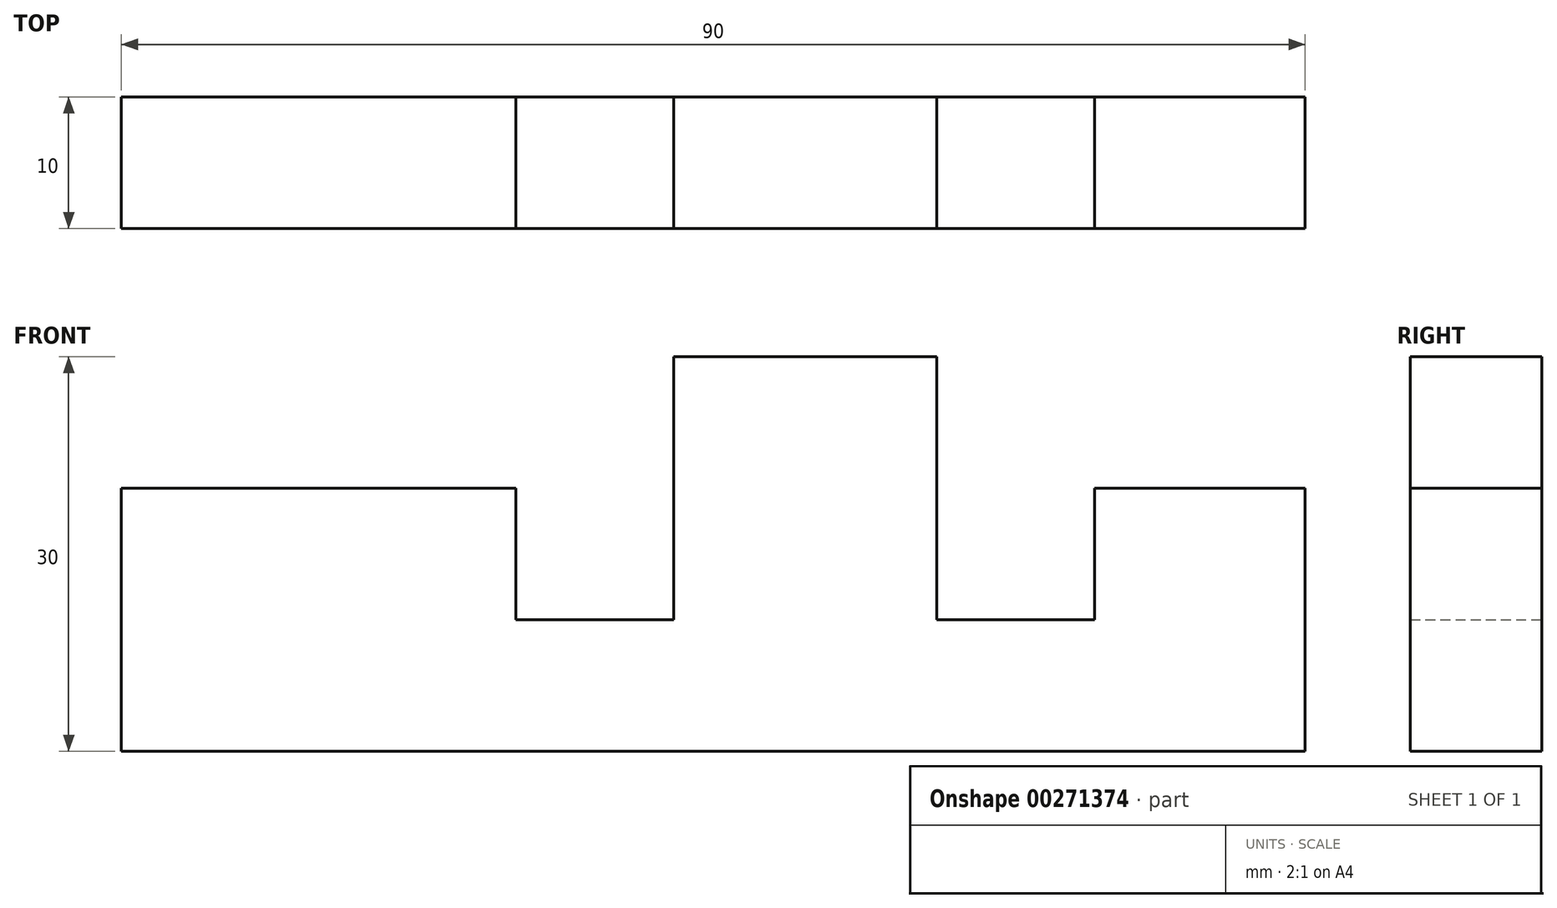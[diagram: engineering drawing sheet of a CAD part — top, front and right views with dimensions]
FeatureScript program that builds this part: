
annotation { "Feature Type Name" : "Feature", "Feature Type Description" : "" }
export const myFeature = defineFeature(function(context is Context, id is Id, definition is map)
    precondition{}
    {
        {
            var Q0;
            Q0=qCreatedBy(makeId("Front.planeOp"),FACE);
            var sketch = newSketch(context, id + "F0", { "sketchPlane" : qUnion([Q0])});
            skLineSegment(sketch, "E0", {"start": v(0, 0) * mm, "end": v(90, 0) * mm});
            skLineSegment(sketch, "E1", {"start": v(0, 0) * mm, "end": v(0, 20) * mm});
            skLineSegment(sketch, "E2", {"start": v(0, 20) * mm, "end": v(30, 20) * mm});
            skLineSegment(sketch, "E3", {"start": v(30, 20) * mm, "end": v(30, 10) * mm});
            skLineSegment(sketch, "E4", {"start": v(30, 10) * mm, "end": v(42, 10) * mm});
            skLineSegment(sketch, "E5", {"start": v(42, 10) * mm, "end": v(42, 30) * mm});
            skLineSegment(sketch, "E6", {"start": v(42, 30) * mm, "end": v(62, 30) * mm});
            skLineSegment(sketch, "E7", {"start": v(62, 30) * mm, "end": v(62, 10) * mm});
            skLineSegment(sketch, "E8", {"start": v(62, 10) * mm, "end": v(74, 10) * mm});
            skLineSegment(sketch, "E9", {"start": v(74, 10) * mm, "end": v(74, 20) * mm});
            skLineSegment(sketch, "E10", {"start": v(90, 0) * mm, "end": v(90, 20) * mm});
            skLineSegment(sketch, "E11", {"start": v(74, 20) * mm, "end": v(90, 20) * mm});
            skSolve(sketch);
        }
        {
            var Q0;
            Q0=makeQuery(id+"F0.imprint","IMPRINT",FACE,{"disambiguationData":[TD([[makeQuery(id+"F0.imprint","IMPRINT",EDGE,{"derivedFrom":sQuery(id+"F0.wireOp",EDGE,"E0")}),1.0]])]});
            extrude(context, id + "F1", {"entities" : qUnion([Q0]), "depth" : 10 * mm});
        }
    });
